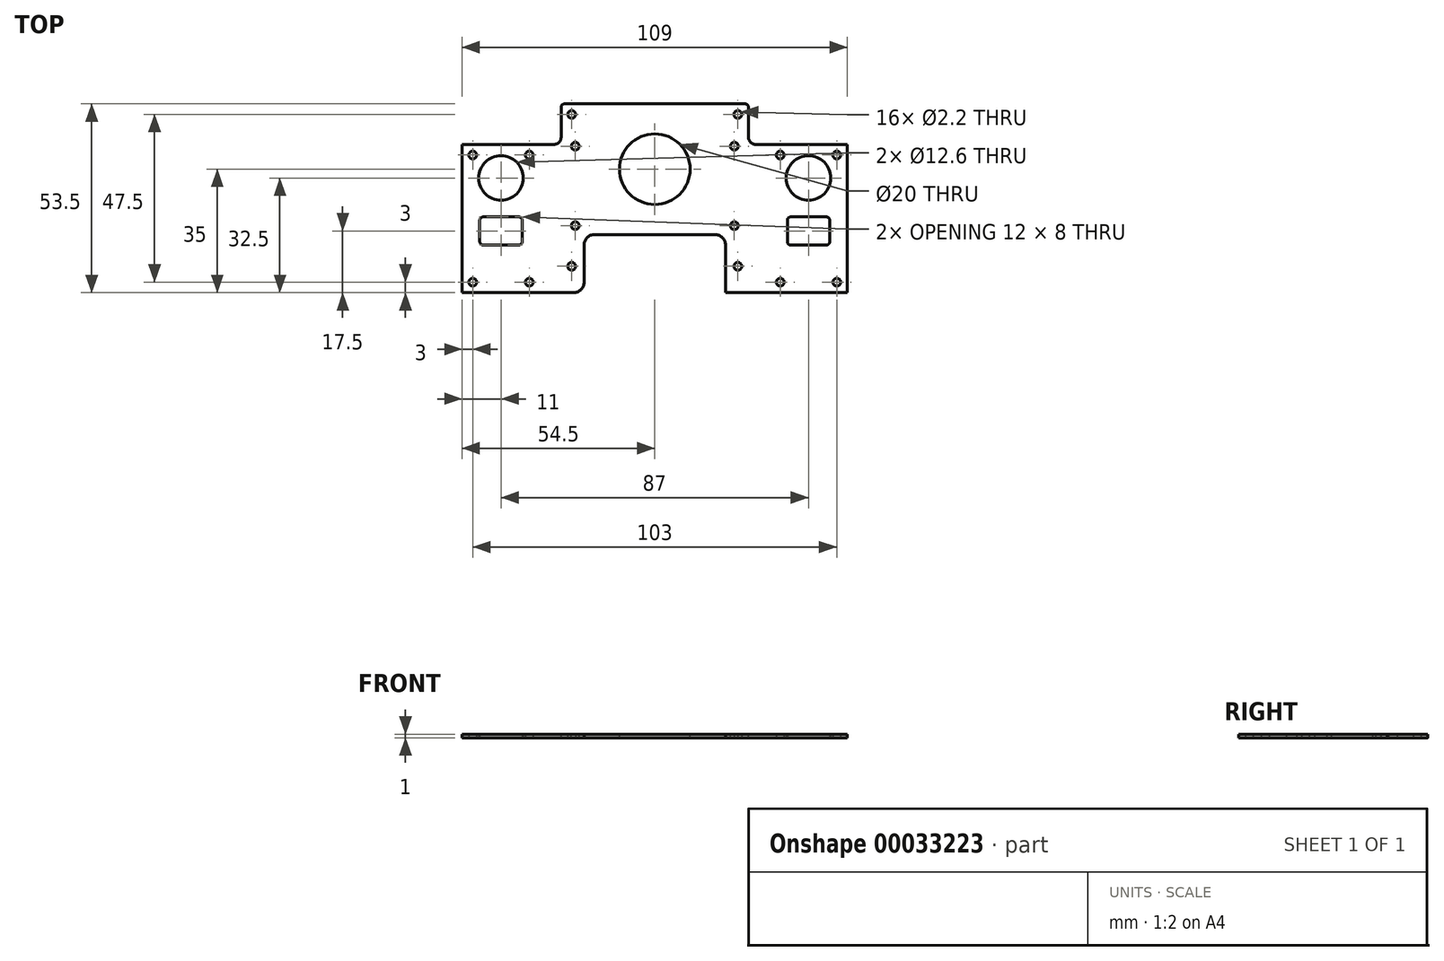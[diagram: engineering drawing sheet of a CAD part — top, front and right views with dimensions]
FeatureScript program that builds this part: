
annotation { "Feature Type Name" : "Feature", "Feature Type Description" : "" }
export const myFeature = defineFeature(function(context is Context, id is Id, definition is map)
    precondition{}
    {
        {
            var Q0;
            Q0=qCreatedBy(makeId("Top.planeOp"),FACE);
            var sketch = newSketch(context, id + "F0", { "sketchPlane" : qUnion([Q0])});
            skLineSegment(sketch, "E0.bottom", {"start": v(-54.5, 35) * mm, "end": v(54.5, 35) * mm});
            skLineSegment(sketch, "E0.top", {"start": v(-54.5, -35) * mm, "end": v(54.5, -35) * mm});
            skLineSegment(sketch, "E0.left", {"start": v(-54.5, 35) * mm, "end": v(-54.5, -35) * mm});
            skLineSegment(sketch, "E0.right", {"start": v(54.5, 35) * mm, "end": v(54.5, -35) * mm});
            skPoint(sketch, "E0.middle", {"position": v(0, 0) * mm});
            skLineSegment(sketch, "E1", {"start": v(-43.5, 35) * mm, "end": v(-43.5, -35) * mm, "construction": true});
            skCircle(sketch, "E2", {"center": v(-51.5, 10) * mm, "radius": 1.1 * mm});
            skCircle(sketch, "E3", {"center": v(-51.5, -26) * mm, "radius": 1.1 * mm});
            skCircle(sketch, "E4.MirrorC", {"center": v(-35.5, 10) * mm, "radius": 1.1 * mm});
            skCircle(sketch, "E5.MirrorC", {"center": v(-35.5, -26) * mm, "radius": 1.1 * mm});
            skCircle(sketch, "E6", {"center": v(-43.5, 3.5) * mm, "radius": 6.3 * mm});
            skCircle(sketch, "E7.MirrorC", {"center": v(35.5, -26) * mm, "radius": 1.1 * mm});
            skCircle(sketch, "E8.MirrorC", {"center": v(43.5, 3.5) * mm, "radius": 6.3 * mm});
            skCircle(sketch, "E9.MirrorC", {"center": v(35.5, 10) * mm, "radius": 1.1 * mm});
            skCircle(sketch, "E10.MirrorC", {"center": v(51.5, 10) * mm, "radius": 1.1 * mm});
            skCircle(sketch, "E11.MirrorC", {"center": v(51.5, -26) * mm, "radius": 1.1 * mm});
            skLineSegment(sketch, "E12.bottom", {"start": v(-38.5, -15.5) * mm, "end": v(-48.5, -15.5) * mm});
            skLineSegment(sketch, "E12.top", {"start": v(-38.5, -7.5) * mm, "end": v(-48.5, -7.5) * mm});
            skLineSegment(sketch, "E12.left", {"start": v(-37.5, -14.5) * mm, "end": v(-37.5, -8.5) * mm});
            skLineSegment(sketch, "E12.right", {"start": v(-49.5, -14.5) * mm, "end": v(-49.5, -8.5) * mm});
            skPoint(sketch, "E12.middle", {"position": v(-43.5, -11.5) * mm});
            skPoint(sketch, "E13.visualSharp", {"position": v(-49.5, -7.5) * mm});
            skArc(sketch, "E13.filletArc", {"start": v(-48.5, -7.5) * mm, "mid": v(-49.2, -7.8) * mm, "end": v(-49.5, -8.5) * mm});
            skPoint(sketch, "E14.visualSharp", {"position": v(-49.5, -15.5) * mm});
            skArc(sketch, "E14.filletArc", {"start": v(-49.5, -14.5) * mm, "mid": v(-49.2, -15.2) * mm, "end": v(-48.5, -15.5) * mm});
            skPoint(sketch, "E15.visualSharp", {"position": v(-37.5, -15.5) * mm});
            skArc(sketch, "E15.filletArc", {"start": v(-38.5, -15.5) * mm, "mid": v(-37.8, -15.2) * mm, "end": v(-37.5, -14.5) * mm});
            skPoint(sketch, "E16.visualSharp", {"position": v(-37.5, -7.5) * mm});
            skArc(sketch, "E16.filletArc", {"start": v(-37.5, -8.5) * mm, "mid": v(-37.8, -7.8) * mm, "end": v(-38.5, -7.5) * mm});
            skArc(sketch, "E17.MirrorCS", {"start": v(48.5, -7.5) * mm, "mid": v(49.2, -7.8) * mm, "end": v(49.5, -8.5) * mm});
            skArc(sketch, "E18.MirrorCS", {"start": v(38.5, -15.5) * mm, "mid": v(37.8, -15.2) * mm, "end": v(37.5, -14.5) * mm});
            skArc(sketch, "E19.MirrorCS", {"start": v(37.5, -8.5) * mm, "mid": v(37.8, -7.8) * mm, "end": v(38.5, -7.5) * mm});
            skArc(sketch, "E20.MirrorCS", {"start": v(49.5, -14.5) * mm, "mid": v(49.2, -15.2) * mm, "end": v(48.5, -15.5) * mm});
            skLineSegment(sketch, "E21.MirrorCS", {"start": v(49.5, -14.5) * mm, "end": v(49.5, -8.5) * mm});
            skLineSegment(sketch, "E22.MirrorCS", {"start": v(38.5, -15.5) * mm, "end": v(48.5, -15.5) * mm});
            skPoint(sketch, "E23.MirrorP", {"position": v(37.5, -15.5) * mm});
            skPoint(sketch, "E24.MirrorP", {"position": v(49.5, -15.5) * mm});
            skPoint(sketch, "E25.MirrorP", {"position": v(49.5, -7.5) * mm});
            skPoint(sketch, "E26.MirrorP", {"position": v(43.5, -11.5) * mm});
            skLineSegment(sketch, "E27.MirrorCS", {"start": v(38.5, -7.5) * mm, "end": v(48.5, -7.5) * mm});
            skLineSegment(sketch, "E28.MirrorCS", {"start": v(37.5, -14.5) * mm, "end": v(37.5, -8.5) * mm});
            skPoint(sketch, "E29.MirrorP", {"position": v(37.5, -7.5) * mm});
            skLineSegment(sketch, "E30", {"start": v(-32.5, 35) * mm, "end": v(-32.5, -35) * mm, "construction": true});
            skArc(sketch, "E31.MirrorCS", {"start": v(-27.5, -8.5) * mm, "mid": v(-27.2, -7.8) * mm, "end": v(-26.5, -7.5) * mm, "construction": true});
            skArc(sketch, "E32.MirrorCS", {"start": v(-15.5, -14.5) * mm, "mid": v(-15.8, -15.2) * mm, "end": v(-16.5, -15.5) * mm, "construction": true});
            skArc(sketch, "E33.MirrorCS", {"start": v(-26.5, -15.5) * mm, "mid": v(-27.2, -15.2) * mm, "end": v(-27.5, -14.5) * mm, "construction": true});
            skArc(sketch, "E34.MirrorCS", {"start": v(-16.5, -7.5) * mm, "mid": v(-15.8, -7.8) * mm, "end": v(-15.5, -8.5) * mm, "construction": true});
            skCircle(sketch, "E35.MirrorC", {"center": v(-13.5, -26) * mm, "radius": 1.1 * mm, "construction": true});
            skCircle(sketch, "E36.MirrorC", {"center": v(-29.5, 10) * mm, "radius": 1.1 * mm, "construction": true});
            skCircle(sketch, "E37.MirrorC", {"center": v(-29.5, -26) * mm, "radius": 1.1 * mm, "construction": true});
            skLineSegment(sketch, "E38.MirrorCS", {"start": v(-15.5, -14.5) * mm, "end": v(-15.5, -8.5) * mm, "construction": true});
            skCircle(sketch, "E39.MirrorC", {"center": v(-21.5, 3.5) * mm, "radius": 6.3 * mm, "construction": true});
            skLineSegment(sketch, "E40.MirrorCS", {"start": v(-26.5, -7.5) * mm, "end": v(-16.5, -7.5) * mm, "construction": true});
            skPoint(sketch, "E41.MirrorP", {"position": v(-21.5, -11.5) * mm});
            skLineSegment(sketch, "E42.MirrorCS", {"start": v(-27.5, -14.5) * mm, "end": v(-27.5, -8.5) * mm, "construction": true});
            skPoint(sketch, "E43.MirrorP", {"position": v(-15.5, -15.5) * mm});
            skPoint(sketch, "E44.MirrorP", {"position": v(-15.5, -7.5) * mm});
            skLineSegment(sketch, "E45.MirrorCS", {"start": v(-26.5, -15.5) * mm, "end": v(-16.5, -15.5) * mm, "construction": true});
            skPoint(sketch, "E46.MirrorP", {"position": v(-27.5, -15.5) * mm});
            skPoint(sketch, "E47.MirrorP", {"position": v(-27.5, -7.5) * mm});
            skCircle(sketch, "E48.MirrorC", {"center": v(-13.5, 10) * mm, "radius": 1.1 * mm, "construction": true});
            skArc(sketch, "E49.MirrorCS", {"start": v(15.5, -14.5) * mm, "mid": v(15.8, -15.2) * mm, "end": v(16.5, -15.5) * mm, "construction": true});
            skArc(sketch, "E50.MirrorCS", {"start": v(26.5, -15.5) * mm, "mid": v(27.2, -15.2) * mm, "end": v(27.5, -14.5) * mm, "construction": true});
            skArc(sketch, "E51.MirrorCS", {"start": v(16.5, -7.5) * mm, "mid": v(15.8, -7.8) * mm, "end": v(15.5, -8.5) * mm, "construction": true});
            skArc(sketch, "E52.MirrorCS", {"start": v(27.5, -8.5) * mm, "mid": v(27.2, -7.8) * mm, "end": v(26.5, -7.5) * mm, "construction": true});
            skLineSegment(sketch, "E53.MirrorCS", {"start": v(15.5, -14.5) * mm, "end": v(15.5, -8.5) * mm, "construction": true});
            skLineSegment(sketch, "E54.MirrorCS", {"start": v(26.5, -15.5) * mm, "end": v(16.5, -15.5) * mm, "construction": true});
            skLineSegment(sketch, "E55.MirrorCS", {"start": v(27.5, -14.5) * mm, "end": v(27.5, -8.5) * mm, "construction": true});
            skPoint(sketch, "E56.MirrorP", {"position": v(15.5, -15.5) * mm});
            skPoint(sketch, "E57.MirrorP", {"position": v(15.5, -7.5) * mm});
            skCircle(sketch, "E58.MirrorC", {"center": v(13.5, -26) * mm, "radius": 1.1 * mm, "construction": true});
            skPoint(sketch, "E59.MirrorP", {"position": v(27.5, -7.5) * mm});
            skCircle(sketch, "E60.MirrorC", {"center": v(13.5, 10) * mm, "radius": 1.1 * mm, "construction": true});
            skLineSegment(sketch, "E61.MirrorCS", {"start": v(26.5, -7.5) * mm, "end": v(16.5, -7.5) * mm, "construction": true});
            skPoint(sketch, "E62.MirrorP", {"position": v(27.5, -15.5) * mm});
            skPoint(sketch, "E63.MirrorP", {"position": v(21.5, -11.5) * mm});
            skCircle(sketch, "E64.MirrorC", {"center": v(21.5, 3.5) * mm, "radius": 6.3 * mm, "construction": true});
            skCircle(sketch, "E65.MirrorC", {"center": v(29.5, 10) * mm, "radius": 1.1 * mm, "construction": true});
            skCircle(sketch, "E66", {"center": v(-23.5, 21.5) * mm, "radius": 1.1 * mm});
            skCircle(sketch, "E67.MirrorC", {"center": v(23.5, 21.5) * mm, "radius": 1.1 * mm});
            skCircle(sketch, "E68.MirrorC", {"center": v(-23.5, -21.5) * mm, "radius": 1.1 * mm});
            skCircle(sketch, "E69.MirrorC", {"center": v(23.5, -21.5) * mm, "radius": 1.1 * mm});
            skSolve(sketch);
        }
        {
            var Q0;
            Q0=qSketchRegion(id+"F0",true);
            extrude(context, id + "F1", {"entities" : qUnion([Q0]), "depth" : 1 * mm});
        }
        {
            var Q0;
            Q0=makeQuery(id+"F1.opExtrude","CAP_FACE",FACE,{"disambiguationData":[OSD([sQuery(id+"F0.wireOp",EDGE,"E0.bottom"),sQuery(id+"F0.wireOp",EDGE,"E0.top"),sQuery(id+"F0.wireOp",EDGE,"E0.left"),sQuery(id+"F0.wireOp",EDGE,"E0.right"),sQuery(id+"F0.wireOp",EDGE,"E2"),sQuery(id+"F0.wireOp",EDGE,"E3"),sQuery(id+"F0.wireOp",EDGE,"E4.MirrorC"),sQuery(id+"F0.wireOp",EDGE,"E5.MirrorC"),sQuery(id+"F0.wireOp",EDGE,"E6"),sQuery(id+"F0.wireOp",EDGE,"E7.MirrorC"),sQuery(id+"F0.wireOp",EDGE,"E8.MirrorC"),sQuery(id+"F0.wireOp",EDGE,"E9.MirrorC"),sQuery(id+"F0.wireOp",EDGE,"E10.MirrorC"),sQuery(id+"F0.wireOp",EDGE,"E11.MirrorC"),sQuery(id+"F0.wireOp",EDGE,"E12.bottom"),sQuery(id+"F0.wireOp",EDGE,"E12.top"),sQuery(id+"F0.wireOp",EDGE,"E12.left"),sQuery(id+"F0.wireOp",EDGE,"E12.right"),sQuery(id+"F0.wireOp",EDGE,"E13.filletArc"),sQuery(id+"F0.wireOp",EDGE,"E14.filletArc"),sQuery(id+"F0.wireOp",EDGE,"E15.filletArc"),sQuery(id+"F0.wireOp",EDGE,"E16.filletArc"),sQuery(id+"F0.wireOp",EDGE,"E17.MirrorCS"),sQuery(id+"F0.wireOp",EDGE,"E18.MirrorCS"),sQuery(id+"F0.wireOp",EDGE,"E19.MirrorCS"),sQuery(id+"F0.wireOp",EDGE,"E20.MirrorCS"),sQuery(id+"F0.wireOp",EDGE,"E21.MirrorCS"),sQuery(id+"F0.wireOp",EDGE,"E22.MirrorCS"),sQuery(id+"F0.wireOp",EDGE,"E27.MirrorCS"),sQuery(id+"F0.wireOp",EDGE,"E28.MirrorCS"),sQuery(id+"F0.wireOp",EDGE,"E66"),sQuery(id+"F0.wireOp",EDGE,"E67.MirrorC"),sQuery(id+"F0.wireOp",EDGE,"E68.MirrorC"),sQuery(id+"F0.wireOp",EDGE,"E69.MirrorC")])],"isStart":false});
            var sketch = newSketch(context, id + "F2", { "sketchPlane" : qUnion([Q0])});
            skLineSegment(sketch, "E70.bottom", {"start": v(-54.5, 35) * mm, "end": v(-26.5, 35) * mm});
            skLineSegment(sketch, "E70.top", {"start": v(-54.5, 13) * mm, "end": v(-28.5, 13) * mm});
            skLineSegment(sketch, "E70.left", {"start": v(-54.5, 35) * mm, "end": v(-54.5, 13) * mm});
            skLineSegment(sketch, "E70.right", {"start": v(-26.5, 35) * mm, "end": v(-26.5, 15) * mm});
            skPoint(sketch, "E71", {"position": v(-23.5, 21.5) * mm});
            skPoint(sketch, "E72", {"position": v(-35.5, 10) * mm});
            skLineSegment(sketch, "E73.MirrorCS", {"start": v(54.5, 13) * mm, "end": v(28.5, 13) * mm});
            skLineSegment(sketch, "E74.MirrorCS", {"start": v(54.5, 35) * mm, "end": v(26.5, 35) * mm});
            skPoint(sketch, "E75.MirrorP", {"position": v(23.5, 21.5) * mm});
            skLineSegment(sketch, "E76.MirrorCS", {"start": v(26.5, 35) * mm, "end": v(26.5, 15) * mm});
            skLineSegment(sketch, "E77.MirrorCS", {"start": v(54.5, 35) * mm, "end": v(54.5, 13) * mm});
            skPoint(sketch, "E78.MirrorP", {"position": v(35.5, 10) * mm});
            skPoint(sketch, "E79.visualSharp", {"position": v(-26.5, 13) * mm});
            skArc(sketch, "E79.filletArc", {"start": v(-28.5, 13) * mm, "mid": v(-27.09, 13.59) * mm, "end": v(-26.5, 15) * mm});
            skPoint(sketch, "E80.visualSharp", {"position": v(26.5, 13) * mm});
            skArc(sketch, "E80.filletArc", {"start": v(26.5, 15) * mm, "mid": v(27.09, 13.59) * mm, "end": v(28.5, 13) * mm});
            skLineSegment(sketch, "E81.bottom", {"start": v(-26.5, 35) * mm, "end": v(26.5, 35) * mm});
            skLineSegment(sketch, "E81.top", {"start": v(-26.5, 24.5) * mm, "end": v(26.5, 24.5) * mm});
            skLineSegment(sketch, "E81.left", {"start": v(-26.5, 35) * mm, "end": v(-26.5, 24.5) * mm});
            skLineSegment(sketch, "E81.right", {"start": v(26.5, 35) * mm, "end": v(26.5, 24.5) * mm});
            skSolve(sketch);
        }
        {
            var Q0;
            Q0=qSketchRegion(id+"F2",true);
            extrude(context, id + "F3", {"entities" : qUnion([Q0]), "operationType" : NewBodyOperationType.REMOVE, "endBound" : BoundingType.UP_TO_NEXT, "oppositeDirection" : true, "depth" : 25 * mm});
        }
        {
            var Q0;
            Q0=makeQuery(id+"F1.opExtrude","CAP_FACE",FACE,{"disambiguationData":[OSD([sQuery(id+"F0.wireOp",EDGE,"E0.bottom"),sQuery(id+"F0.wireOp",EDGE,"E0.top"),sQuery(id+"F0.wireOp",EDGE,"E0.left"),sQuery(id+"F0.wireOp",EDGE,"E0.right"),sQuery(id+"F0.wireOp",EDGE,"E2"),sQuery(id+"F0.wireOp",EDGE,"E3"),sQuery(id+"F0.wireOp",EDGE,"E4.MirrorC"),sQuery(id+"F0.wireOp",EDGE,"E5.MirrorC"),sQuery(id+"F0.wireOp",EDGE,"E6"),sQuery(id+"F0.wireOp",EDGE,"E7.MirrorC"),sQuery(id+"F0.wireOp",EDGE,"E8.MirrorC"),sQuery(id+"F0.wireOp",EDGE,"E9.MirrorC"),sQuery(id+"F0.wireOp",EDGE,"E10.MirrorC"),sQuery(id+"F0.wireOp",EDGE,"E11.MirrorC"),sQuery(id+"F0.wireOp",EDGE,"E12.bottom"),sQuery(id+"F0.wireOp",EDGE,"E12.top"),sQuery(id+"F0.wireOp",EDGE,"E12.left"),sQuery(id+"F0.wireOp",EDGE,"E12.right"),sQuery(id+"F0.wireOp",EDGE,"E13.filletArc"),sQuery(id+"F0.wireOp",EDGE,"E14.filletArc"),sQuery(id+"F0.wireOp",EDGE,"E15.filletArc"),sQuery(id+"F0.wireOp",EDGE,"E16.filletArc"),sQuery(id+"F0.wireOp",EDGE,"E17.MirrorCS"),sQuery(id+"F0.wireOp",EDGE,"E18.MirrorCS"),sQuery(id+"F0.wireOp",EDGE,"E19.MirrorCS"),sQuery(id+"F0.wireOp",EDGE,"E20.MirrorCS"),sQuery(id+"F0.wireOp",EDGE,"E21.MirrorCS"),sQuery(id+"F0.wireOp",EDGE,"E22.MirrorCS"),sQuery(id+"F0.wireOp",EDGE,"E27.MirrorCS"),sQuery(id+"F0.wireOp",EDGE,"E28.MirrorCS"),sQuery(id+"F0.wireOp",EDGE,"E66"),sQuery(id+"F0.wireOp",EDGE,"E67.MirrorC"),sQuery(id+"F0.wireOp",EDGE,"E68.MirrorC"),sQuery(id+"F0.wireOp",EDGE,"E69.MirrorC")])],"isStart":false});
            var sketch = newSketch(context, id + "F4", { "sketchPlane" : qUnion([Q0])});
            skLineSegment(sketch, "E82.bottom", {"start": v(-54.5, -35) * mm, "end": v(0, -35) * mm});
            skLineSegment(sketch, "E82.top", {"start": v(-54.5, -29) * mm, "end": v(0, -29) * mm});
            skLineSegment(sketch, "E82.left", {"start": v(-54.5, -35) * mm, "end": v(-54.5, -29) * mm});
            skPoint(sketch, "E83", {"position": v(-51.5, -26) * mm});
            skLineSegment(sketch, "E84.MirrorCS", {"start": v(54.5, -35) * mm, "end": v(0, -35) * mm});
            skLineSegment(sketch, "E85.MirrorCS", {"start": v(54.5, -29) * mm, "end": v(0, -29) * mm});
            skLineSegment(sketch, "E86.MirrorCS", {"start": v(54.5, -35) * mm, "end": v(54.5, -29) * mm});
            skSolve(sketch);
        }
        {
            var Q0;
            Q0=qSketchRegion(id+"F4",true);
            extrude(context, id + "F5", {"entities" : qUnion([Q0]), "operationType" : NewBodyOperationType.REMOVE, "endBound" : BoundingType.UP_TO_NEXT, "oppositeDirection" : true, "depth" : 25 * mm});
        }
        {
            var Q0;
            Q0=makeQuery(id+"F5.boolean.opBoolean","COPY",EDGE,{"derivedFrom":makeQuery(id+"F5.opExtrude","SWEPT_EDGE",EDGE,{"disambiguationData":[OSD([sQuery(id+"F0.wireOp",EDGE,"E0.left"),sQuery(id+"F4.wireOp",EDGE,"E82.top"),sQuery(id+"F4.wireOp",EDGE,"E82.left")])]})});
            var Q1;
            Q1=makeQuery(id+"F5.boolean.opBoolean","COPY",EDGE,{"derivedFrom":makeQuery(id+"F5.opExtrude","SWEPT_EDGE",EDGE,{"disambiguationData":[OSD([sQuery(id+"F2.wireOp",EDGE,"bq7dnykM-F30T-xU7x-uZbt-F96BpZRt0wA2.right"),sQuery(id+"F4.wireOp",EDGE,"E82.top"),sQuery(id+"F4.wireOp",EDGE,"E82.right")])]})});
            var Q2;
            Q2=makeQuery(id+"F5.boolean.opBoolean","COPY",EDGE,{"derivedFrom":makeQuery(id+"F5.opExtrude","SWEPT_EDGE",EDGE,{"disambiguationData":[OSD([sQuery(id+"F2.wireOp",EDGE,"bq7dnykM-F30T-xU7x-uZbt-F96BpZRt0wA2.left"),sQuery(id+"F4.wireOp",EDGE,"E85.MirrorCS"),sQuery(id+"F4.wireOp",EDGE,"5f0d883e-aae6-4400-8f53-724f4b6b7ac63.MirrorCS")])]})});
            var Q3;
            Q3=makeQuery(id+"F5.boolean.opBoolean","COPY",EDGE,{"derivedFrom":makeQuery(id+"F5.opExtrude","SWEPT_EDGE",EDGE,{"disambiguationData":[OSD([sQuery(id+"F0.wireOp",EDGE,"E0.right"),sQuery(id+"F4.wireOp",EDGE,"E85.MirrorCS"),sQuery(id+"F4.wireOp",EDGE,"E86.MirrorCS")])]})});
            var Q4;
            Q4=makeQuery(id+"F3.boolean.opBoolean","COPY",EDGE,{"derivedFrom":makeQuery(id+"F3.opExtrude","SWEPT_EDGE",EDGE,{"disambiguationData":[OSD([sQuery(id+"F2.wireOp",EDGE,"bq7dnykM-F30T-xU7x-uZbt-F96BpZRt0wA2.top"),sQuery(id+"F2.wireOp",EDGE,"bq7dnykM-F30T-xU7x-uZbt-F96BpZRt0wA2.right")])]})});
            var Q5;
            Q5=makeQuery(id+"F3.boolean.opBoolean","COPY",EDGE,{"derivedFrom":makeQuery(id+"F3.opExtrude","SWEPT_EDGE",EDGE,{"disambiguationData":[OSD([sQuery(id+"F2.wireOp",EDGE,"bq7dnykM-F30T-xU7x-uZbt-F96BpZRt0wA2.top"),sQuery(id+"F2.wireOp",EDGE,"bq7dnykM-F30T-xU7x-uZbt-F96BpZRt0wA2.left")])]})});
            var Q6;
            Q6=makeQuery(id+"F3.boolean.opBoolean","COPY",EDGE,{"derivedFrom":makeQuery(id+"F3.opExtrude","SWEPT_EDGE",EDGE,{"disambiguationData":[OSD([sQuery(id+"F0.wireOp",EDGE,"E0.right"),sQuery(id+"F2.wireOp",EDGE,"E73.MirrorCS"),sQuery(id+"F2.wireOp",EDGE,"E77.MirrorCS")])]})});
            var Q7;
            Q7=makeQuery(id+"F3.boolean.opBoolean","COPY",EDGE,{"derivedFrom":makeQuery(id+"F3.opExtrude","SWEPT_EDGE",EDGE,{"disambiguationData":[OSD([sQuery(id+"F2.wireOp",EDGE,"E76.MirrorCS"),sQuery(id+"F2.wireOp",EDGE,"E81.top"),sQuery(id+"F2.wireOp",EDGE,"E81.right")])]})});
            var Q8;
            Q8=makeQuery(id+"F3.boolean.opBoolean","COPY",EDGE,{"derivedFrom":makeQuery(id+"F3.opExtrude","SWEPT_EDGE",EDGE,{"disambiguationData":[OSD([sQuery(id+"F2.wireOp",EDGE,"E70.right"),sQuery(id+"F2.wireOp",EDGE,"E81.top"),sQuery(id+"F2.wireOp",EDGE,"E81.left")])]})});
            var Q9;
            Q9=makeQuery(id+"F3.boolean.opBoolean","COPY",EDGE,{"derivedFrom":makeQuery(id+"F3.opExtrude","SWEPT_EDGE",EDGE,{"disambiguationData":[OSD([sQuery(id+"F0.wireOp",EDGE,"E0.left"),sQuery(id+"F2.wireOp",EDGE,"E70.top"),sQuery(id+"F2.wireOp",EDGE,"E70.left")])]})});
            fillet(context, id + "F6", {"entities" : qUnion([Q0, Q1, Q2, Q3, Q4, Q5, Q6, Q7, Q8, Q9]), "radius" : 1 * mm, "tangentPropagation" : true, "allowEdgeOverflow" : false});
        }
        {
            var Q0;
            Q0=makeQuery(id+"F1.opExtrude","CAP_FACE",FACE,{"disambiguationData":[OSD([sQuery(id+"F0.wireOp",EDGE,"E0.bottom"),sQuery(id+"F0.wireOp",EDGE,"E0.top"),sQuery(id+"F0.wireOp",EDGE,"E0.left"),sQuery(id+"F0.wireOp",EDGE,"E0.right"),sQuery(id+"F0.wireOp",EDGE,"E2"),sQuery(id+"F0.wireOp",EDGE,"E3"),sQuery(id+"F0.wireOp",EDGE,"E4.MirrorC"),sQuery(id+"F0.wireOp",EDGE,"E5.MirrorC"),sQuery(id+"F0.wireOp",EDGE,"E6"),sQuery(id+"F0.wireOp",EDGE,"E7.MirrorC"),sQuery(id+"F0.wireOp",EDGE,"E8.MirrorC"),sQuery(id+"F0.wireOp",EDGE,"E9.MirrorC"),sQuery(id+"F0.wireOp",EDGE,"E10.MirrorC"),sQuery(id+"F0.wireOp",EDGE,"E11.MirrorC"),sQuery(id+"F0.wireOp",EDGE,"E12.bottom"),sQuery(id+"F0.wireOp",EDGE,"E12.top"),sQuery(id+"F0.wireOp",EDGE,"E12.left"),sQuery(id+"F0.wireOp",EDGE,"E12.right"),sQuery(id+"F0.wireOp",EDGE,"E13.filletArc"),sQuery(id+"F0.wireOp",EDGE,"E14.filletArc"),sQuery(id+"F0.wireOp",EDGE,"E15.filletArc"),sQuery(id+"F0.wireOp",EDGE,"E16.filletArc"),sQuery(id+"F0.wireOp",EDGE,"E17.MirrorCS"),sQuery(id+"F0.wireOp",EDGE,"E18.MirrorCS"),sQuery(id+"F0.wireOp",EDGE,"E19.MirrorCS"),sQuery(id+"F0.wireOp",EDGE,"E20.MirrorCS"),sQuery(id+"F0.wireOp",EDGE,"E21.MirrorCS"),sQuery(id+"F0.wireOp",EDGE,"E22.MirrorCS"),sQuery(id+"F0.wireOp",EDGE,"E27.MirrorCS"),sQuery(id+"F0.wireOp",EDGE,"E28.MirrorCS"),sQuery(id+"F0.wireOp",EDGE,"E66"),sQuery(id+"F0.wireOp",EDGE,"E67.MirrorC"),sQuery(id+"F0.wireOp",EDGE,"E68.MirrorC"),sQuery(id+"F0.wireOp",EDGE,"E69.MirrorC")])],"isStart":false});
            var sketch = newSketch(context, id + "F7", { "sketchPlane" : qUnion([Q0])});
            skCircle(sketch, "E87", {"center": v(-22.5, -10) * mm, "radius": 1.1 * mm});
            skCircle(sketch, "E88.MirrorC", {"center": v(22.5, -10) * mm, "radius": 1.1 * mm});
            skCircle(sketch, "E89", {"center": v(-22.5, 12.5) * mm, "radius": 1.1 * mm});
            skCircle(sketch, "E90.MirrorC", {"center": v(22.5, 12.5) * mm, "radius": 1.1 * mm});
            skLineSegment(sketch, "E91.bottom", {"start": v(20, -29) * mm, "end": v(-20, -29) * mm});
            skLineSegment(sketch, "E91.top", {"start": v(20, -12.5) * mm, "end": v(-20, -12.5) * mm});
            skLineSegment(sketch, "E91.left", {"start": v(20, -29) * mm, "end": v(20, -12.5) * mm});
            skLineSegment(sketch, "E91.right", {"start": v(-20, -29) * mm, "end": v(-20, -12.5) * mm});
            skPoint(sketch, "E91.middle", {"position": v(0, -20.75) * mm});
            skCircle(sketch, "E92", {"center": v(0, 6) * mm, "radius": 10 * mm});
            skLineSegment(sketch, "E93", {"start": v(0, 24.5) * mm, "end": v(0, -12.5) * mm, "construction": true});
            skLineSegment(sketch, "E94", {"start": v(-22.5, 12.5) * mm, "end": v(-22.5, -10) * mm, "construction": true});
            skPoint(sketch, "E95", {"position": v(-22.5, 1.25) * mm});
            skSolve(sketch);
        }
        {
            var Q0;
            Q0 = qSketchRegion(id + "F7", true);
            extrude(context, id + "F8", {"entities" : qUnion([Q0]), "operationType" : NewBodyOperationType.REMOVE, "endBound" : BoundingType.UP_TO_NEXT, "oppositeDirection" : true, "depth" : 25 * mm});
        }
        {
            var Q0;
            Q0=makeQuery(id+"F8.boolean.opBoolean","COPY",EDGE,{"derivedFrom":makeQuery(id+"F8.opExtrude","SWEPT_EDGE",EDGE,{"disambiguationData":[OSD([sQuery(id+"F4.wireOp",EDGE,"E82.top"),sQuery(id+"F4.wireOp",EDGE,"E85.MirrorCS"),sQuery(id+"F7.wireOp",EDGE,"E91.bottom"),sQuery(id+"F7.wireOp",EDGE,"E91.right")])]})});
            var Q1;
            Q1=makeQuery(id+"F8.boolean.opBoolean","COPY",EDGE,{"derivedFrom":makeQuery(id+"F8.opExtrude","SWEPT_EDGE",EDGE,{"disambiguationData":[OSD([sQuery(id+"F7.wireOp",EDGE,"E91.top"),sQuery(id+"F7.wireOp",EDGE,"E91.right")])]})});
            var Q2;
            Q2=makeQuery(id+"F8.boolean.opBoolean","COPY",EDGE,{"derivedFrom":makeQuery(id+"F8.opExtrude","SWEPT_EDGE",EDGE,{"disambiguationData":[OSD([sQuery(id+"F7.wireOp",EDGE,"E91.top"),sQuery(id+"F7.wireOp",EDGE,"E91.left")])]})});
            var Q3;
            Q3=makeQuery(id+"F8.boolean.opBoolean","COPY",EDGE,{"derivedFrom":makeQuery(id+"F8.opExtrude","SWEPT_EDGE",EDGE,{"disambiguationData":[OSD([sQuery(id+"F4.wireOp",EDGE,"E82.top"),sQuery(id+"F4.wireOp",EDGE,"E85.MirrorCS"),sQuery(id+"F7.wireOp",EDGE,"E91.bottom"),sQuery(id+"F7.wireOp",EDGE,"E91.left")])]})});
            fillet(context, id + "F9", {"entities" : qUnion([Q0, Q1, Q2, Q3]), "radius" : 3 * mm, "tangentPropagation" : true, "allowEdgeOverflow" : false});
        }
    });
